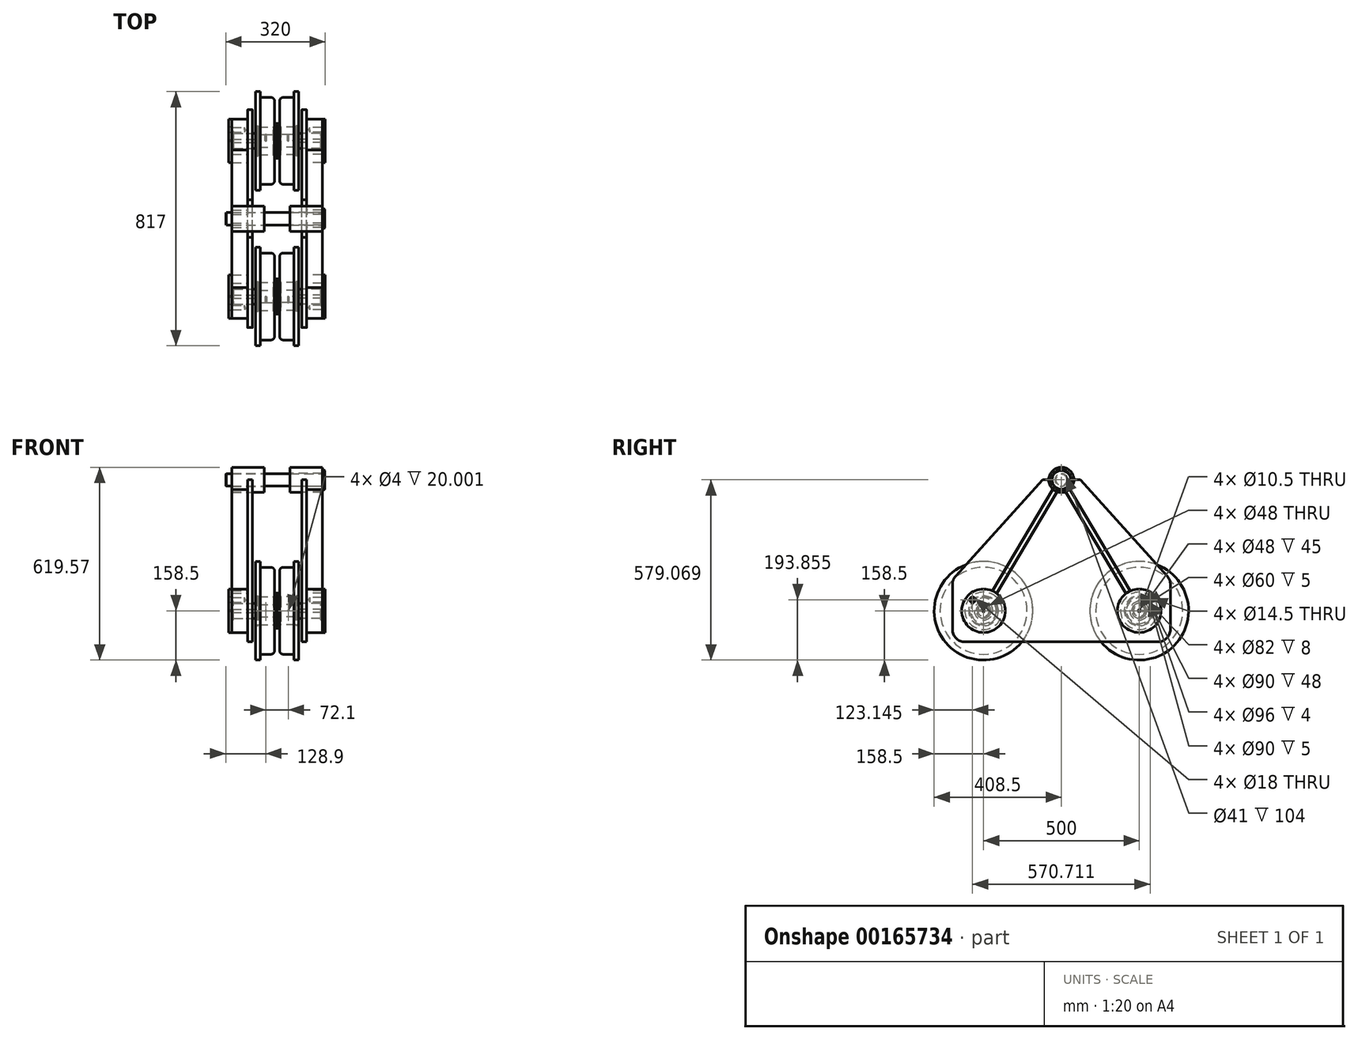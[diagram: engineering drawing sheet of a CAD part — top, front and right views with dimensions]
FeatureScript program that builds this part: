
annotation { "Feature Type Name" : "Feature", "Feature Type Description" : "" }
export const myFeature = defineFeature(function(context is Context, id is Id, definition is map)
    precondition{}
    {
        {
            var Q0;
            Q0=qCreatedBy(makeId("Front.planeOp"),FACE);
            var sketch = newSketch(context, id + "F0", { "sketchPlane" : qUnion([Q0])});
            skLineSegment(sketch, "E0", {"start": v(0, 214.58) * mm, "end": v(0, -214.58) * mm, "construction": true});
            skLineSegment(sketch, "E1", {"start": v(-51, 153.5) * mm, "end": v(-51, 141.7) * mm});
            skLineSegment(sketch, "E2", {"start": v(-51, 141.7) * mm, "end": v(-11.95, 141.7) * mm});
            skLineSegment(sketch, "E3", {"start": v(-3.05, 132.8) * mm, "end": v(-3.05, -132.8) * mm});
            skLineSegment(sketch, "E4", {"start": v(-11.95, -141.7) * mm, "end": v(-51, -141.7) * mm});
            skLineSegment(sketch, "E5", {"start": v(-51, -141.7) * mm, "end": v(-51, -153.5) * mm});
            skLineSegment(sketch, "E6", {"start": v(-51, -153.5) * mm, "end": v(51, -153.5) * mm});
            skLineSegment(sketch, "E7", {"start": v(51, -153.5) * mm, "end": v(51, -141.7) * mm});
            skLineSegment(sketch, "E8", {"start": v(51, -141.7) * mm, "end": v(11.95, -141.7) * mm});
            skLineSegment(sketch, "E9", {"start": v(3.05, -132.8) * mm, "end": v(3.05, 132.8) * mm});
            skLineSegment(sketch, "E10", {"start": v(11.95, 141.7) * mm, "end": v(51, 141.7) * mm});
            skLineSegment(sketch, "E11", {"start": v(51, 141.7) * mm, "end": v(51, 153.5) * mm});
            skLineSegment(sketch, "E12", {"start": v(51, 153.5) * mm, "end": v(-51, 153.5) * mm});
            skPoint(sketch, "E13.visualSharp", {"position": v(-3.05, 141.7) * mm});
            skArc(sketch, "E13.filletArc", {"start": v(-3.05, 132.8) * mm, "mid": v(-5.66, 139.1) * mm, "end": v(-11.95, 141.7) * mm});
            skPoint(sketch, "E14.visualSharp", {"position": v(3.05, 141.7) * mm});
            skArc(sketch, "E14.filletArc", {"start": v(11.95, 141.7) * mm, "mid": v(5.66, 139.1) * mm, "end": v(3.05, 132.8) * mm});
            skPoint(sketch, "E15.visualSharp", {"position": v(3.05, -141.7) * mm});
            skArc(sketch, "E15.filletArc", {"start": v(3.05, -132.8) * mm, "mid": v(5.66, -139.1) * mm, "end": v(11.95, -141.7) * mm});
            skPoint(sketch, "E16.visualSharp", {"position": v(-3.05, -141.7) * mm});
            skArc(sketch, "E16.filletArc", {"start": v(-11.95, -141.7) * mm, "mid": v(-5.66, -139.1) * mm, "end": v(-3.05, -132.8) * mm});
            skLineSegment(sketch, "E17", {"start": v(-117.48, 0) * mm, "end": v(187.6, 0) * mm, "construction": true});
            skLineSegment(sketch, "E18", {"start": v(54, 158.5) * mm, "end": v(54, 139.7) * mm});
            skLineSegment(sketch, "E19", {"start": v(54, 139.7) * mm, "end": v(20.05, 139.7) * mm});
            skLineSegment(sketch, "E20", {"start": v(8.05, 127.7) * mm, "end": v(8.05, 60) * mm});
            skLineSegment(sketch, "E21", {"start": v(8.05, 60) * mm, "end": v(4.05, 60) * mm});
            skLineSegment(sketch, "E22", {"start": v(4.05, 60) * mm, "end": v(4.05, 41) * mm});
            skLineSegment(sketch, "E23", {"start": v(4.05, 41) * mm, "end": v(12.05, 41) * mm});
            skLineSegment(sketch, "E24", {"start": v(12.05, 41) * mm, "end": v(12.05, 45) * mm});
            skLineSegment(sketch, "E25", {"start": v(12.05, 45) * mm, "end": v(60.05, 45) * mm});
            skLineSegment(sketch, "E26", {"start": v(60.05, 45) * mm, "end": v(60.05, 48) * mm});
            skLineSegment(sketch, "E27", {"start": v(60.05, 48) * mm, "end": v(64.05, 48) * mm});
            skLineSegment(sketch, "E28", {"start": v(64.05, 48) * mm, "end": v(64.05, 45) * mm});
            skLineSegment(sketch, "E29", {"start": v(64.05, 45) * mm, "end": v(69.05, 45) * mm});
            skLineSegment(sketch, "E30", {"start": v(54, 158.5) * mm, "end": v(69.05, 158.5) * mm});
            skLineSegment(sketch, "E31", {"start": v(69.05, 158.5) * mm, "end": v(69.05, 45) * mm});
            skPoint(sketch, "E32.visualSharp", {"position": v(8.05, 139.7) * mm});
            skArc(sketch, "E32.filletArc", {"start": v(20.05, 139.7) * mm, "mid": v(11.56, 136.19) * mm, "end": v(8.05, 127.7) * mm});
            skLineSegment(sketch, "E33", {"start": v(8.05, 0) * mm, "end": v(8.05, 20) * mm});
            skLineSegment(sketch, "E34", {"start": v(8.05, 20) * mm, "end": v(60.05, 20) * mm});
            skLineSegment(sketch, "E35", {"start": v(60.05, 20) * mm, "end": v(60.05, 24) * mm});
            skLineSegment(sketch, "E36", {"start": v(60.05, 24) * mm, "end": v(140.05, 24) * mm});
            skLineSegment(sketch, "E37", {"start": v(140.05, 24) * mm, "end": v(140.05, 30) * mm});
            skLineSegment(sketch, "E38", {"start": v(140.05, 30) * mm, "end": v(145.05, 30) * mm});
            skLineSegment(sketch, "E39", {"start": v(145.05, 30) * mm, "end": v(145.05, 0) * mm});
            skLineSegment(sketch, "E40", {"start": v(145.05, 0) * mm, "end": v(8.05, 0) * mm});
            skPoint(sketch, "E41", {"position": v(36.05, 0) * mm});
            skPoint(sketch, "E42", {"position": v(36.05, 45) * mm});
            skSolve(sketch);
        }
        {
            var Q0;
            Q0=makeQuery(id+"F0.imprint","IMPRINT",FACE,{"disambiguationData":[TD([[makeQuery(id+"F0.imprint","IMPRINT",EDGE,{"derivedFrom":sQuery(id+"F0.wireOp",EDGE,"E18")}),1.0]])]});
            var Q1;
            Q1=sQuery(id+"F0.wireOp",EDGE,"E17");
            revolve(context, id + "F1", {"entities" : qUnion([Q0]), "axis" : qUnion([Q1]), "revolveType" : RevolveType.FULL});
        }
        {
            var Q0;
            Q0=makeQuery(id+"F0.imprint","IMPRINT",FACE,{"disambiguationData":[TD([[makeQuery(id+"F0.imprint","IMPRINT",EDGE,{"derivedFrom":sQuery(id+"F0.wireOp",EDGE,"E33")}),-1.0]])]});
            var Q1;
            Q1=sQuery(id+"F0.wireOp",EDGE,"E17");
            revolve(context, id + "F2", {"entities" : qUnion([Q0]), "axis" : qUnion([Q1]), "revolveType" : RevolveType.FULL});
        }
        {
            var Q0;
            Q0=makeQuery(id+"F2.opRevolve","SWEPT_EDGE",EDGE,{"disambiguationData":[OSD([sQuery(id+"F0.wireOp",EDGE,"E33"),sQuery(id+"F0.wireOp",EDGE,"E34")])]});
            chamfer(context, id + "F3", {"entities" : qUnion([Q0]), "width" : 2 * mm, "tangentPropagation" : true});
        }
        {
            var Q0;
            Q0=makeQuery(id+"F2.opRevolve","SWEPT_EDGE",EDGE,{"disambiguationData":[OSD([sQuery(id+"F0.wireOp",EDGE,"E37"),sQuery(id+"F0.wireOp",EDGE,"E38")])]});
            var Q1;
            Q1=makeQuery(id+"F2.opRevolve","SWEPT_EDGE",EDGE,{"disambiguationData":[OSD([sQuery(id+"F0.wireOp",EDGE,"E38"),sQuery(id+"F0.wireOp",EDGE,"E39")])]});
            chamfer(context, id + "F4", {"entities" : qUnion([Q0, Q1]), "width" : 1 * mm, "tangentPropagation" : true});
        }
        {
            var Q0;
            Q0=makeQuery(id+"F2.opRevolve","SWEPT_FACE",FACE,{"disambiguationData":[OSD([sQuery(id+"F0.wireOp",EDGE,"E39")])]});
            var sketch = newSketch(context, id + "F5", { "sketchPlane" : qUnion([Q0])});
            skPoint(sketch, "E43", {"position": v(0, 0) * mm});
            skSolve(sketch);
        }
        {
            var Q0;
            Q0=sQuery(id+"F5.wireOp",VERTEX,"E43");
            var Q1;
            Q1=makeQuery(id+"F2.opRevolve","SWEPT_BODY",BODY,{"disambiguationData":[OSD([sQuery(id+"F0.wireOp",EDGE,"E33"),sQuery(id+"F0.wireOp",EDGE,"E34"),sQuery(id+"F0.wireOp",EDGE,"E35"),sQuery(id+"F0.wireOp",EDGE,"E36"),sQuery(id+"F0.wireOp",EDGE,"E37"),sQuery(id+"F0.wireOp",EDGE,"E38"),sQuery(id+"F0.wireOp",EDGE,"E39"),sQuery(id+"F0.wireOp",EDGE,"E40")])]});
            hole(context, id + "F6", {"style" : HoleStyle.SIMPLE, "endStyle" : HoleEndStyle.BLIND, "standardTappedOrClearance" : lookupTablePath({ "standard" : "ISO", "size" : "4", "type" : "Drilled" }), "standardBlindInLast" : lookupTablePath({ "standard" : "ISO", "size" : "4", "type" : "Drilled" }), "holeDiameter" : 4 * mm, "holeDepth" : 80 * mm, "locations" : qUnion([Q0]), "scope" : qUnion([Q1])});
        }
        {
            var Q0;
            Q0=sQuery(id+"F5.wireOp",VERTEX,"E43");
            var Q1;
            Q1=makeQuery(id+"F2.opRevolve","SWEPT_BODY",BODY,{"disambiguationData":[OSD([sQuery(id+"F0.wireOp",EDGE,"E33"),sQuery(id+"F0.wireOp",EDGE,"E34"),sQuery(id+"F0.wireOp",EDGE,"E35"),sQuery(id+"F0.wireOp",EDGE,"E36"),sQuery(id+"F0.wireOp",EDGE,"E37"),sQuery(id+"F0.wireOp",EDGE,"E38"),sQuery(id+"F0.wireOp",EDGE,"E39"),sQuery(id+"F0.wireOp",EDGE,"E40")])]});
            hole(context, id + "F7", {"style" : HoleStyle.SIMPLE, "endStyle" : HoleEndStyle.BLIND, "standardTappedOrClearance" : lookupTablePath({ "standard" : "ISO", "engagement" : "75%", "pitch" : "1.5 mm", "size" : "M12", "type" : "Tapped" }), "standardBlindInLast" : lookupTablePath({ "standard" : "ISO", "engagement" : "75%", "pitch" : "1.5 mm", "size" : "M12", "type" : "Tapped" }), "holeDiameter" : 10.5 * mm, "holeDepth" : 10 * mm, "locations" : qUnion([Q0]), "scope" : qUnion([Q1]), "majorDiameter" : 12 * mm});
        }
        {
            var Q0;
            Q0=sQuery(id+"F0.wireOp",VERTEX,"E41");
            var Q1;
            Q1=makeQuery(id+"F2.opRevolve","SWEPT_BODY",BODY,{"disambiguationData":[OSD([sQuery(id+"F0.wireOp",EDGE,"E33"),sQuery(id+"F0.wireOp",EDGE,"E34"),sQuery(id+"F0.wireOp",EDGE,"E35"),sQuery(id+"F0.wireOp",EDGE,"E36"),sQuery(id+"F0.wireOp",EDGE,"E37"),sQuery(id+"F0.wireOp",EDGE,"E38"),sQuery(id+"F0.wireOp",EDGE,"E39"),sQuery(id+"F0.wireOp",EDGE,"E40")])]});
            hole(context, id + "F8", {"style" : HoleStyle.SIMPLE, "endStyle" : HoleEndStyle.THROUGH, "oppositeDirection" : true, "standardTappedOrClearance" : lookupTablePath({ "standard" : "ISO", "size" : "4", "type" : "Drilled" }), "standardBlindInLast" : lookupTablePath({ "standard" : "ISO", "size" : "4", "type" : "Drilled" }), "holeDiameter" : 4 * mm, "locations" : qUnion([Q0]), "scope" : qUnion([Q1]), "isTappedThrough" : true});
        }
        {
            var Q0;
            Q0=makeQuery(id+"F1.opRevolve","SWEPT_FACE",FACE,{"disambiguationData":[OSD([sQuery(id+"F0.wireOp",EDGE,"E31")])]});
            cPlane(context, id + "F9", {"entities" : qUnion([Q0]), "cplaneType" : CPlaneType.OFFSET, "offset" : 10 * mm, "width" : 150 * mm, "height" : 150 * mm});
        }
        {
            var Q0;
            Q0=qCreatedBy(id+"F9.planeOp",FACE);
            var sketch = newSketch(context, id + "F10", { "sketchPlane" : qUnion([Q0])});
            skLineSegment(sketch, "E44", {"start": v(-60, -100) * mm, "end": v(560, -100) * mm});
            skLineSegment(sketch, "E45", {"start": v(600, -60) * mm, "end": v(600, 84.61) * mm});
            skLineSegment(sketch, "E46", {"start": v(589.69, 111.42) * mm, "end": v(310.5, 420.57) * mm});
            skPoint(sketch, "E46.endSnap0", {"position": v(250, -100) * mm});
            skLineSegment(sketch, "E47", {"start": v(189.5, 420.57) * mm, "end": v(-89.69, 111.42) * mm});
            skLineSegment(sketch, "E48", {"start": v(-100, 84.61) * mm, "end": v(-100, -60) * mm});
            skCircle(sketch, "E49", {"center": v(0, 0) * mm, "radius": 24 * mm});
            skPoint(sketch, "E50.visualSharp", {"position": v(-100, -100) * mm});
            skArc(sketch, "E50.filletArc", {"start": v(-100, -60) * mm, "mid": v(-88.28, -88.28) * mm, "end": v(-60, -100) * mm});
            skPoint(sketch, "E51.visualSharp", {"position": v(600, -100) * mm});
            skArc(sketch, "E51.filletArc", {"start": v(560, -100) * mm, "mid": v(588.28, -88.28) * mm, "end": v(600, -60) * mm});
            skCircle(sketch, "E52", {"center": v(500, 0) * mm, "radius": 24 * mm});
            skLineSegment(sketch, "E53", {"start": v(250, 487.56) * mm, "end": v(250, -100) * mm, "construction": true});
            skPoint(sketch, "E54.visualSharp", {"position": v(-100, 100) * mm});
            skArc(sketch, "E54.filletArc", {"start": v(-89.69, 111.42) * mm, "mid": v(-97.33, 98.97) * mm, "end": v(-100, 84.61) * mm});
            skPoint(sketch, "E55.visualSharp", {"position": v(600, 100) * mm});
            skArc(sketch, "E55.filletArc", {"start": v(600, 84.61) * mm, "mid": v(597.33, 98.97) * mm, "end": v(589.69, 111.42) * mm});
            skArc(sketch, "E56", {"start": v(209.5, 420.57) * mm, "mid": v(250, 380.07) * mm, "end": v(290.5, 420.57) * mm});
            skLineSegment(sketch, "E57", {"start": v(209.5, 420.57) * mm, "end": v(189.5, 420.57) * mm});
            skLineSegment(sketch, "E58", {"start": v(290.5, 420.57) * mm, "end": v(310.5, 420.57) * mm});
            skSolve(sketch);
        }
        {
            var Q0;
            Q0=makeQuery(id+"F10.imprint","IMPRINT",FACE,{"disambiguationData":[TD([[makeQuery(id+"F10.imprint","IMPRINT",EDGE,{"derivedFrom":sQuery(id+"F10.wireOp",EDGE,"E44")}),1.0]])]});
            extrude(context, id + "F11", {"entities" : qUnion([Q0]), "depth" : 16 * mm});
        }
        {
            var Q0;
            Q0=makeQuery(id+"F11.opExtrude","CAP_FACE",FACE,{"disambiguationData":[OSD([sQuery(id+"F10.wireOp",EDGE,"E44"),sQuery(id+"F10.wireOp",EDGE,"E45"),sQuery(id+"F10.wireOp",EDGE,"E46"),sQuery(id+"F10.wireOp",EDGE,"E47"),sQuery(id+"F10.wireOp",EDGE,"E48"),sQuery(id+"F10.wireOp",EDGE,"E49"),sQuery(id+"F10.wireOp",EDGE,"E50.filletArc"),sQuery(id+"F10.wireOp",EDGE,"E51.filletArc"),sQuery(id+"F10.wireOp",EDGE,"E52"),sQuery(id+"F10.wireOp",EDGE,"E54.filletArc"),sQuery(id+"F10.wireOp",EDGE,"E55.filletArc"),sQuery(id+"F10.wireOp",EDGE,"E56"),sQuery(id+"F10.wireOp",EDGE,"E57"),sQuery(id+"F10.wireOp",EDGE,"E58")])],"isStart":false});
            var sketch = newSketch(context, id + "F12", { "sketchPlane" : qUnion([Q0])});
            skCircle(sketch, "E59", {"center": v(0, 0) * mm, "radius": 70 * mm});
            skCircle(sketch, "E60", {"center": v(250, 420.57) * mm, "radius": 40.5 * mm});
            skCircle(sketch, "E61", {"center": v(250, 420.57) * mm, "radius": 20.5 * mm});
            skLineSegment(sketch, "E62", {"start": v(0, 0) * mm, "end": v(250, 420.57) * mm, "construction": true});
            skLineSegment(sketch, "E63", {"start": v(28.9, 64.26) * mm, "end": v(222.43, 389.84) * mm});
            skLineSegment(sketch, "E64", {"start": v(222.43, 389.84) * mm, "end": v(236.18, 381.67) * mm});
            skLineSegment(sketch, "E65", {"start": v(236.18, 381.67) * mm, "end": v(42.64, 56.08) * mm});
            skLineSegment(sketch, "E66", {"start": v(42.64, 56.08) * mm, "end": v(28.9, 64.26) * mm});
            skPoint(sketch, "E67", {"position": v(35.77, 60.17) * mm});
            skPoint(sketch, "E68", {"position": v(229.3, 385.76) * mm});
            skSolve(sketch);
        }
        {
            var Q0;
            Q0=makeQuery(id+"F12.imprint","IMPRINT",FACE,{"disambiguationData":[TD([[makeQuery(id+"F12.imprint","IMPRINT",EDGE,{"derivedFrom":sQuery(id+"F12.wireOp",EDGE,"E59")}),1.0]])]});
            extrude(context, id + "F13", {"entities" : qUnion([Q0]), "depth" : 50 * mm});
        }
        {
            var Q0;
            Q0=makeQuery(id+"F13.opExtrude","CAP_FACE",FACE,{"disambiguationData":[OSD([sQuery(id+"F10.wireOp",EDGE,"E49"),sQuery(id+"F12.wireOp",EDGE,"E59")])],"isStart":false});
            var sketch = newSketch(context, id + "F14", { "sketchPlane" : qUnion([Q0])});
            skCircle(sketch, "E69", {"center": v(0, 0) * mm, "radius": 50 * mm, "construction": true});
            skPoint(sketch, "E70", {"position": v(-35.36, 35.36) * mm});
            skLineSegment(sketch, "E71", {"start": v(-35.36, 35.36) * mm, "end": v(0, 0) * mm, "construction": true});
            skCircle(sketch, "E72", {"center": v(0, 0) * mm, "radius": 30 * mm});
            skSolve(sketch);
        }
        {
            var Q0;
            Q0=makeQuery(id+"F14.imprint","IMPRINT",FACE,{"disambiguationData":[TD([[makeQuery(id+"F14.imprint","IMPRINT",EDGE,{"derivedFrom":sQuery(id+"F14.wireOp",EDGE,"E72")}),1.0]])]});
            extrude(context, id + "F15", {"entities" : qUnion([Q0]), "operationType" : NewBodyOperationType.REMOVE, "oppositeDirection" : true, "depth" : 5 * mm});
        }
        {
            var Q0;
            Q0=makeQuery(id+"F14.imprint","IMPRINT",FACE,{"disambiguationData":[TD([[makeQuery(id+"F14.imprint","IMPRINT",EDGE,{"derivedFrom":sQuery(id+"F14.wireOp",EDGE,"E72")}),-1.0]])]});
            var Q1;
            Q1=makeQuery(id+"F14.imprint","IMPRINT",FACE,{"disambiguationData":[TD([[makeQuery(id+"F14.imprint","IMPRINT",EDGE,{"derivedFrom":sQuery(id+"F14.wireOp",EDGE,"E72")}),1.0]])]});
            var Q2;
            Q2=makeQuery(id+"F14.imprint","IMPRINT",FACE,{"disambiguationData":[TD([[makeQuery(id+"F14.imprint","IMPRINT",EDGE,{"derivedFrom":makeQuery(id+"F13.opExtrude","CAP_EDGE",EDGE,{"disambiguationData":[OSD([sQuery(id+"F10.wireOp",EDGE,"E49")])],"isStart":false})}),1.0]])]});
            extrude(context, id + "F16", {"entities" : qUnion([Q0, Q1, Q2]), "depth" : 10 * mm});
        }
        {
            var Q0;
            Q0=sQuery(id+"F14.wireOp",VERTEX,"E70");
            var Q1;
            Q1=makeQuery(id+"F13.opExtrude","SWEPT_BODY",BODY,{"disambiguationData":[OSD([sQuery(id+"F10.wireOp",EDGE,"E49"),sQuery(id+"F12.wireOp",EDGE,"E59")])]});
            hole(context, id + "F17", {"style" : HoleStyle.SIMPLE, "endStyle" : HoleEndStyle.BLIND, "standardTappedOrClearance" : lookupTablePath({ "standard" : "ISO", "engagement" : "75%", "pitch" : "1.5 mm", "size" : "M16", "type" : "Tapped" }), "standardBlindInLast" : lookupTablePath({ "standard" : "ISO", "engagement" : "75%", "pitch" : "1.5 mm", "size" : "M16", "type" : "Tapped" }), "holeDiameter" : 14.5 * mm, "holeDepth" : 40 * mm, "locations" : qUnion([Q0]), "scope" : qUnion([Q1]), "majorDiameter" : 16 * mm});
        }
        {
            var Q0;
            Q0=sQuery(id+"F14.wireOp",VERTEX,"E70");
            var Q1;
            Q1=makeQuery(id+"F16.opExtrude","SWEPT_BODY",BODY,{"disambiguationData":[OSD([sQuery(id+"F12.wireOp",EDGE,"E59")])]});
            hole(context, id + "F18", {"style" : HoleStyle.SIMPLE, "endStyle" : HoleEndStyle.BLIND, "oppositeDirection" : true, "standardTappedOrClearance" : lookupTablePath({ "standard" : "ISO", "size" : "18", "type" : "Drilled" }), "standardBlindInLast" : lookupTablePath({ "standard" : "ISO", "size" : "18", "type" : "Drilled" }), "holeDiameter" : 18 * mm, "holeDepth" : 40 * mm, "locations" : qUnion([Q0]), "scope" : qUnion([Q1])});
        }
        {
            var Q0;
            Q0=sQuery(id+"F5.wireOp",VERTEX,"E43");
            var Q1;
            Q1=makeQuery(id+"F16.opExtrude","SWEPT_BODY",BODY,{"disambiguationData":[OSD([sQuery(id+"F12.wireOp",EDGE,"E59")])]});
            hole(context, id + "F19", {"style" : HoleStyle.SIMPLE, "endStyle" : HoleEndStyle.THROUGH, "oppositeDirection" : true, "standardTappedOrClearance" : lookupTablePath({ "standard" : "ISO", "engagement" : "75%", "pitch" : "0.75 mm", "size" : "M6", "type" : "Tapped" }), "standardBlindInLast" : lookupTablePath({ "standard" : "ISO", "engagement" : "75%", "pitch" : "0.75 mm", "size" : "M6", "type" : "Tapped" }), "holeDiameter" : 5.25 * mm, "locations" : qUnion([Q0]), "scope" : qUnion([Q1]), "isTappedThrough" : true, "majorDiameter" : 6 * mm, "showTappedDepth" : true});
        }
        {
            var Q0;
            Q0=makeQuery(id+"F12.imprint","IMPRINT",FACE,{"disambiguationData":[TD([[makeQuery(id+"F12.imprint","IMPRINT",EDGE,{"derivedFrom":sQuery(id+"F12.wireOp",EDGE,"E61")}),-1.0]])]});
            extrude(context, id + "F20", {"entities" : qUnion([Q0]), "depth" : 50 * mm, "hasSecondDirection" : true, "secondDirectionOppositeDirection" : true, "secondDirectionDepth" : 54 * mm});
        }
        {
            var Q0;
            {var subQ2=sQuery(id+"F12.wireOp",EDGE,"E63");Q0=makeQuery(id+"F12.imprint","IMPRINT",FACE,{"disambiguationData":[TD([[makeQuery(id+"F12.imprint","IMPRINT",EDGE,{"derivedFrom":subQ2}),-1.0]])]});}
            extrude(context, id + "F21", {"entities" : qUnion([Q0]), "depth" : 50 * mm});
        }
        {
            var Q0;
            Q0=sQuery(id+"F10.wireOp",EDGE,"E44");
            cPoint(context, id + "F22", {"entities" : qUnion([Q0]), "parameter" : 0.5});
        }
        {
            var Q0;
            Q0 = qCreatedBy(id + "F22" ,VERTEX);
            var Q1;
            Q1=sQuery(id+"F10.wireOp",EDGE,"E44");
            cPlane(context, id + "F23", {"entities" : qUnion([Q0, Q1]), "cplaneType" : CPlaneType.LINE_POINT, "offset" : 25 * mm, "width" : 150 * mm, "height" : 150 * mm});
        }
        {
            var Q0;
            Q0=makeQuery(id+"F21.opExtrude","SWEPT_BODY",BODY,{"disambiguationData":[OSD([sQuery(id+"F12.wireOp",EDGE,"E63"),sQuery(id+"F12.wireOp",EDGE,"E64"),sQuery(id+"F12.wireOp",EDGE,"E65"),sQuery(id+"F12.wireOp",EDGE,"E66")])]});
            var Q1;
            Q1=makeQuery(id+"F16.opExtrude","SWEPT_BODY",BODY,{"disambiguationData":[OSD([sQuery(id+"F12.wireOp",EDGE,"E59")])]});
            var Q2;
            Q2=makeQuery(id+"F13.opExtrude","SWEPT_BODY",BODY,{"disambiguationData":[OSD([sQuery(id+"F10.wireOp",EDGE,"E49"),sQuery(id+"F12.wireOp",EDGE,"E59")])]});
            var Q3;
            Q3=makeQuery(id+"F1.opRevolve","SWEPT_BODY",BODY,{"disambiguationData":[OSD([sQuery(id+"F0.wireOp",EDGE,"E18"),sQuery(id+"F0.wireOp",EDGE,"E19"),sQuery(id+"F0.wireOp",EDGE,"E20"),sQuery(id+"F0.wireOp",EDGE,"E21"),sQuery(id+"F0.wireOp",EDGE,"E22"),sQuery(id+"F0.wireOp",EDGE,"E23"),sQuery(id+"F0.wireOp",EDGE,"E24"),sQuery(id+"F0.wireOp",EDGE,"E25"),sQuery(id+"F0.wireOp",EDGE,"E26"),sQuery(id+"F0.wireOp",EDGE,"E27"),sQuery(id+"F0.wireOp",EDGE,"E28"),sQuery(id+"F0.wireOp",EDGE,"E29"),sQuery(id+"F0.wireOp",EDGE,"E30"),sQuery(id+"F0.wireOp",EDGE,"E31"),sQuery(id+"F0.wireOp",EDGE,"E32.filletArc")])]});
            var Q4;
            Q4=makeQuery(id+"F2.opRevolve","SWEPT_BODY",BODY,{"disambiguationData":[OSD([sQuery(id+"F0.wireOp",EDGE,"E33"),sQuery(id+"F0.wireOp",EDGE,"E34"),sQuery(id+"F0.wireOp",EDGE,"E35"),sQuery(id+"F0.wireOp",EDGE,"E36"),sQuery(id+"F0.wireOp",EDGE,"E37"),sQuery(id+"F0.wireOp",EDGE,"E38"),sQuery(id+"F0.wireOp",EDGE,"E39"),sQuery(id+"F0.wireOp",EDGE,"E40")])]});
            var Q5;
            Q5=qCreatedBy(id+"F23.planeOp",FACE);
            mirror(context, id + "F24", {"entities" : qUnion([Q0, Q1, Q2, Q3, Q4]), "mirrorPlane" : qUnion([Q5])});
        }
        {
            var Q0;
            Q0=makeQuery(id+"F20.opExtrude","SWEPT_BODY",BODY,{"disambiguationData":[OSD([sQuery(id+"F12.wireOp",EDGE,"E60"),sQuery(id+"F12.wireOp",EDGE,"E61")])]});
            var Q1;
            Q1=makeQuery(id+"F11.opExtrude","SWEPT_BODY",BODY,{"disambiguationData":[OSD([sQuery(id+"F10.wireOp",EDGE,"E44"),sQuery(id+"F10.wireOp",EDGE,"E45"),sQuery(id+"F10.wireOp",EDGE,"E46"),sQuery(id+"F10.wireOp",EDGE,"E47"),sQuery(id+"F10.wireOp",EDGE,"E48"),sQuery(id+"F10.wireOp",EDGE,"E49"),sQuery(id+"F10.wireOp",EDGE,"E50.filletArc"),sQuery(id+"F10.wireOp",EDGE,"E51.filletArc"),sQuery(id+"F10.wireOp",EDGE,"E52"),sQuery(id+"F10.wireOp",EDGE,"E54.filletArc"),sQuery(id+"F10.wireOp",EDGE,"E55.filletArc"),sQuery(id+"F10.wireOp",EDGE,"E56"),sQuery(id+"F10.wireOp",EDGE,"E57"),sQuery(id+"F10.wireOp",EDGE,"E58")])]});
            var Q2;
            Q2=makeQuery(id+"F24.opPattern","COPY",BODY,{"derivedFrom":makeQuery(id+"F21.opExtrude","SWEPT_BODY",BODY,{"disambiguationData":[OSD([sQuery(id+"F12.wireOp",EDGE,"E63"),sQuery(id+"F12.wireOp",EDGE,"E64"),sQuery(id+"F12.wireOp",EDGE,"E65"),sQuery(id+"F12.wireOp",EDGE,"E66")])]}),"instanceName":"1"});
            var Q3;
            Q3=makeQuery(id+"F21.opExtrude","SWEPT_BODY",BODY,{"disambiguationData":[OSD([sQuery(id+"F12.wireOp",EDGE,"E63"),sQuery(id+"F12.wireOp",EDGE,"E64"),sQuery(id+"F12.wireOp",EDGE,"E65"),sQuery(id+"F12.wireOp",EDGE,"E66")])]});
            var Q4;
            Q4=makeQuery(id+"F16.opExtrude","SWEPT_BODY",BODY,{"disambiguationData":[OSD([sQuery(id+"F12.wireOp",EDGE,"E59")])]});
            var Q5;
            Q5=makeQuery(id+"F13.opExtrude","SWEPT_BODY",BODY,{"disambiguationData":[OSD([sQuery(id+"F10.wireOp",EDGE,"E49"),sQuery(id+"F12.wireOp",EDGE,"E59")])]});
            var Q6;
            Q6=makeQuery(id+"F24.opPattern","COPY",BODY,{"derivedFrom":makeQuery(id+"F16.opExtrude","SWEPT_BODY",BODY,{"disambiguationData":[OSD([sQuery(id+"F12.wireOp",EDGE,"E59")])]}),"instanceName":"1"});
            var Q7;
            Q7=makeQuery(id+"F24.opPattern","COPY",BODY,{"derivedFrom":makeQuery(id+"F13.opExtrude","SWEPT_BODY",BODY,{"disambiguationData":[OSD([sQuery(id+"F10.wireOp",EDGE,"E49"),sQuery(id+"F12.wireOp",EDGE,"E59")])]}),"instanceName":"1"});
            var Q8;
            Q8=makeQuery(id+"F2.opRevolve","SWEPT_BODY",BODY,{"disambiguationData":[OSD([sQuery(id+"F0.wireOp",EDGE,"E33"),sQuery(id+"F0.wireOp",EDGE,"E34"),sQuery(id+"F0.wireOp",EDGE,"E35"),sQuery(id+"F0.wireOp",EDGE,"E36"),sQuery(id+"F0.wireOp",EDGE,"E37"),sQuery(id+"F0.wireOp",EDGE,"E38"),sQuery(id+"F0.wireOp",EDGE,"E39"),sQuery(id+"F0.wireOp",EDGE,"E40")])]});
            var Q9;
            Q9=makeQuery(id+"F24.opPattern","COPY",BODY,{"derivedFrom":makeQuery(id+"F2.opRevolve","SWEPT_BODY",BODY,{"disambiguationData":[OSD([sQuery(id+"F0.wireOp",EDGE,"E33"),sQuery(id+"F0.wireOp",EDGE,"E34"),sQuery(id+"F0.wireOp",EDGE,"E35"),sQuery(id+"F0.wireOp",EDGE,"E36"),sQuery(id+"F0.wireOp",EDGE,"E37"),sQuery(id+"F0.wireOp",EDGE,"E38"),sQuery(id+"F0.wireOp",EDGE,"E39"),sQuery(id+"F0.wireOp",EDGE,"E40")])]}),"instanceName":"1"});
            var Q10;
            Q10=makeQuery(id+"F1.opRevolve","SWEPT_BODY",BODY,{"disambiguationData":[OSD([sQuery(id+"F0.wireOp",EDGE,"E18"),sQuery(id+"F0.wireOp",EDGE,"E19"),sQuery(id+"F0.wireOp",EDGE,"E20"),sQuery(id+"F0.wireOp",EDGE,"E21"),sQuery(id+"F0.wireOp",EDGE,"E22"),sQuery(id+"F0.wireOp",EDGE,"E23"),sQuery(id+"F0.wireOp",EDGE,"E24"),sQuery(id+"F0.wireOp",EDGE,"E25"),sQuery(id+"F0.wireOp",EDGE,"E26"),sQuery(id+"F0.wireOp",EDGE,"E27"),sQuery(id+"F0.wireOp",EDGE,"E28"),sQuery(id+"F0.wireOp",EDGE,"E29"),sQuery(id+"F0.wireOp",EDGE,"E30"),sQuery(id+"F0.wireOp",EDGE,"E31"),sQuery(id+"F0.wireOp",EDGE,"E32.filletArc")])]});
            var Q11;
            Q11=makeQuery(id+"F24.opPattern","COPY",BODY,{"derivedFrom":makeQuery(id+"F1.opRevolve","SWEPT_BODY",BODY,{"disambiguationData":[OSD([sQuery(id+"F0.wireOp",EDGE,"E18"),sQuery(id+"F0.wireOp",EDGE,"E19"),sQuery(id+"F0.wireOp",EDGE,"E20"),sQuery(id+"F0.wireOp",EDGE,"E21"),sQuery(id+"F0.wireOp",EDGE,"E22"),sQuery(id+"F0.wireOp",EDGE,"E23"),sQuery(id+"F0.wireOp",EDGE,"E24"),sQuery(id+"F0.wireOp",EDGE,"E25"),sQuery(id+"F0.wireOp",EDGE,"E26"),sQuery(id+"F0.wireOp",EDGE,"E27"),sQuery(id+"F0.wireOp",EDGE,"E28"),sQuery(id+"F0.wireOp",EDGE,"E29"),sQuery(id+"F0.wireOp",EDGE,"E30"),sQuery(id+"F0.wireOp",EDGE,"E31"),sQuery(id+"F0.wireOp",EDGE,"E32.filletArc")])]}),"instanceName":"1"});
            var Q12;
            Q12=qCreatedBy(makeId("Right.planeOp"),FACE);
            mirror(context, id + "F25", {"entities" : qUnion([Q0, Q1, Q2, Q3, Q4, Q5, Q6, Q7, Q8, Q9, Q10, Q11]), "mirrorPlane" : qUnion([Q12])});
        }
        {
            var Q0;
            Q0=makeQuery(id+"F20.opExtrude","CAP_FACE",FACE,{"disambiguationData":[OSD([sQuery(id+"F12.wireOp",EDGE,"E60"),sQuery(id+"F12.wireOp",EDGE,"E61")])],"isStart":false});
            var sketch = newSketch(context, id + "F26", { "sketchPlane" : qUnion([Q0])});
            skCircle(sketch, "E73", {"center": v(250, 420.57) * mm, "radius": 20 * mm});
            skCircle(sketch, "E74", {"center": v(250, 420.57) * mm, "radius": 32 * mm});
            skSolve(sketch);
        }
        {
            var Q0;
            Q0=makeQuery(id+"F26.imprint","IMPRINT",FACE,{"disambiguationData":[TD([[makeQuery(id+"F26.imprint","IMPRINT",EDGE,{"derivedFrom":sQuery(id+"F26.wireOp",EDGE,"E73")}),1.0]])]});
            extrude(context, id + "F27", {"entities" : qUnion([Q0]), "oppositeDirection" : true, "depth" : 310 * mm});
        }
        {
            var Q0;
            Q0=makeQuery(id+"F26.imprint","IMPRINT",FACE,{"disambiguationData":[TD([[makeQuery(id+"F26.imprint","IMPRINT",EDGE,{"derivedFrom":sQuery(id+"F26.wireOp",EDGE,"E74")}),1.0]])]});
            var Q1;
            Q1=makeQuery(id+"F26.imprint","IMPRINT",FACE,{"disambiguationData":[TD([[makeQuery(id+"F26.imprint","IMPRINT",EDGE,{"derivedFrom":sQuery(id+"F26.wireOp",EDGE,"E73")}),-1.0]])]});
            var Q2;
            Q2=makeQuery(id+"F26.imprint","IMPRINT",FACE,{"disambiguationData":[TD([[makeQuery(id+"F26.imprint","IMPRINT",EDGE,{"derivedFrom":sQuery(id+"F26.wireOp",EDGE,"E73")}),1.0]])]});
            extrude(context, id + "F28", {"entities" : qUnion([Q0, Q1, Q2]), "operationType" : NewBodyOperationType.ADD, "depth" : 8 * mm});
        }
        {
            var Q0;
            Q0=makeQuery(id+"F28.opExtrude","CAP_EDGE",EDGE,{"disambiguationData":[OSD([sQuery(id+"F26.wireOp",EDGE,"E74")])],"isStart":false});
            var Q1;
            Q1=makeQuery(id+"F28.opExtrude","CAP_EDGE",EDGE,{"disambiguationData":[OSD([sQuery(id+"F26.wireOp",EDGE,"E74")])],"isStart":true});
            var Q2;
            Q2=makeQuery(id+"F27.opExtrude","CAP_EDGE",EDGE,{"disambiguationData":[OSD([sQuery(id+"F26.wireOp",EDGE,"E73")])],"isStart":false});
            chamfer(context, id + "F29", {"entities" : qUnion([Q0, Q1, Q2]), "width" : 2 * mm, "tangentPropagation" : true});
        }
    });
